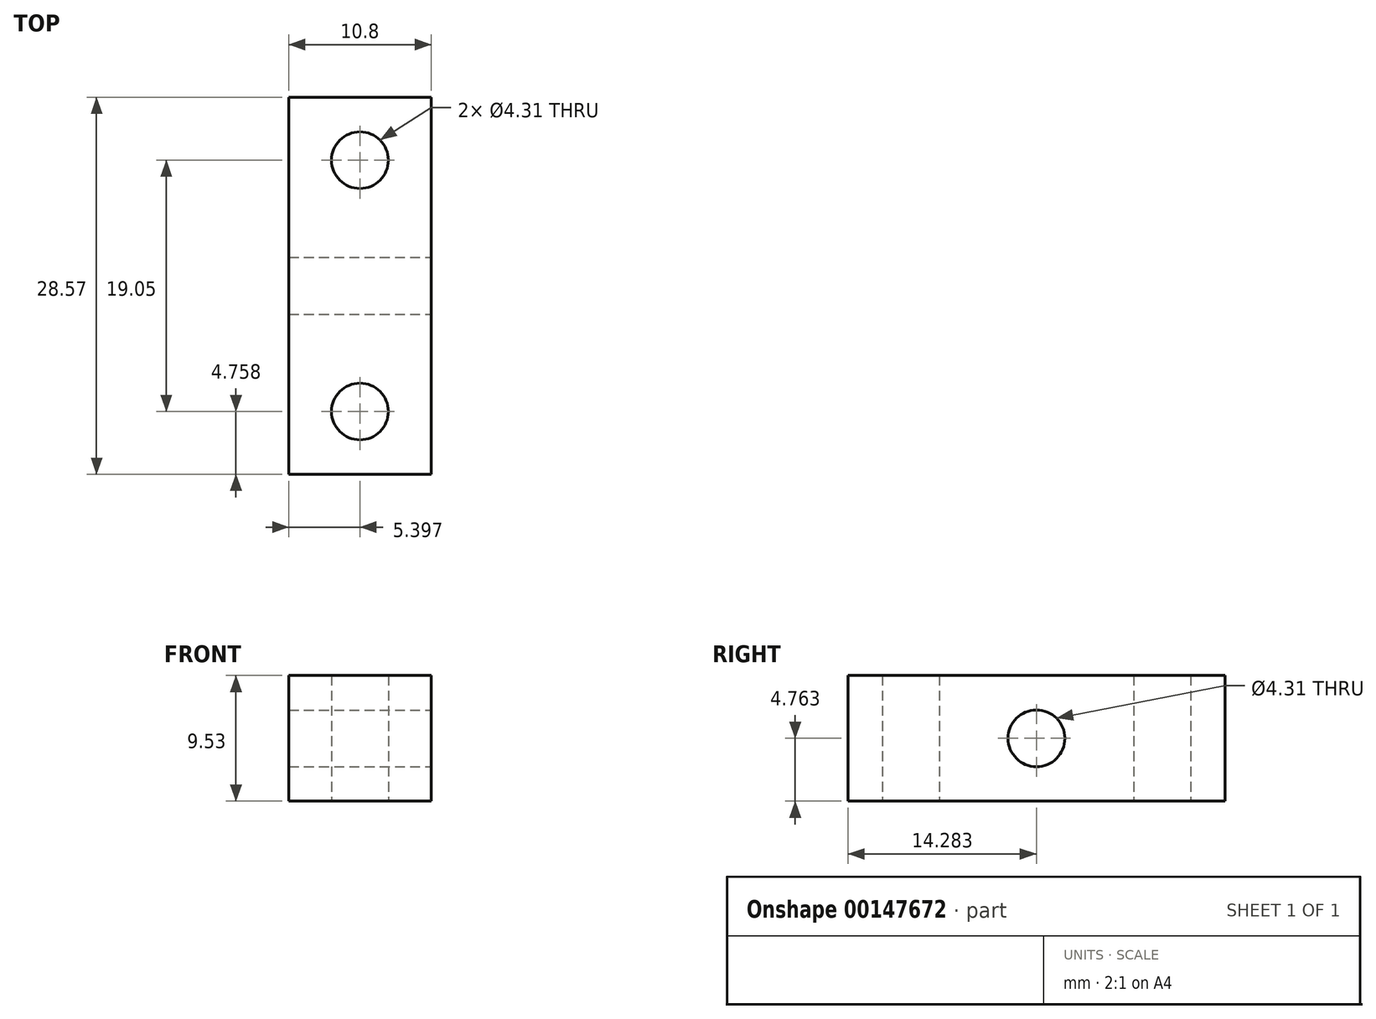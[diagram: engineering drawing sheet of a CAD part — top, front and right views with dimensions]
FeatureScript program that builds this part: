
annotation { "Feature Type Name" : "Feature", "Feature Type Description" : "" }
export const myFeature = defineFeature(function(context is Context, id is Id, definition is map)
    precondition{}
    {
        {
            var Q0;
            Q0=qCreatedBy(makeId("Top.planeOp"),FACE);
            var sketch = newSketch(context, id + "F0", { "sketchPlane" : qUnion([Q0])});
            skLineSegment(sketch, "E0.bottom", {"start": v(0, 0) * mm, "end": v(10.8, 0) * mm});
            skLineSegment(sketch, "E0.top", {"start": v(0, -28.57) * mm, "end": v(10.8, -28.57) * mm});
            skLineSegment(sketch, "E0.left", {"start": v(0, 0) * mm, "end": v(0, -28.57) * mm});
            skLineSegment(sketch, "E0.right", {"start": v(10.8, 0) * mm, "end": v(10.8, -28.57) * mm});
            skLineSegment(sketch, "E1", {"start": v(5.4, 0) * mm, "end": v(5.4, -4.76) * mm, "construction": true});
            skLineSegment(sketch, "E2", {"start": v(5.4, -4.76) * mm, "end": v(5.4, -23.81) * mm, "construction": true});
            skLineSegment(sketch, "E3", {"start": v(5.4, -23.81) * mm, "end": v(5.4, -28.57) * mm, "construction": true});
            skCircle(sketch, "E4", {"center": v(5.4, -4.76) * mm, "radius": 2.15 * mm});
            skCircle(sketch, "E5", {"center": v(5.4, -23.81) * mm, "radius": 2.15 * mm});
            skSolve(sketch);
        }
        {
            var Q0;
            Q0=qSketchRegion(id+"F0",true);
            extrude(context, id + "F1", {"entities" : qUnion([Q0]), "depth" : 9.52 * mm});
        }
        {
            var Q0;
            Q0=makeQuery(id+"F1.opExtrude","SWEPT_FACE",FACE,{"disambiguationData":[OSD([sQuery(id+"F0.wireOp",EDGE,"E0.right")])]});
            var sketch = newSketch(context, id + "F2", { "sketchPlane" : qUnion([Q0])});
            skLineSegment(sketch, "E6", {"start": v(0, 4.76) * mm, "end": v(-14.29, 4.76) * mm, "construction": true});
            skCircle(sketch, "E7", {"center": v(-14.29, 4.76) * mm, "radius": 2.15 * mm});
            skSolve(sketch);
        }
        {
            var Q0;
            Q0=qSketchRegion(id+"F2",true);
            var Q1;
            Q1=makeQuery(id+"F1.opExtrude","SWEPT_FACE",FACE,{"disambiguationData":[OSD([sQuery(id+"F0.wireOp",EDGE,"E0.left")])]});
            extrude(context, id + "F3", {"entities" : qUnion([Q0]), "operationType" : NewBodyOperationType.REMOVE, "endBound" : BoundingType.UP_TO_SURFACE, "oppositeDirection" : true, "endBoundEntityFace" : qUnion([Q1]), "depth" : 25.4 * mm});
        }
    });
